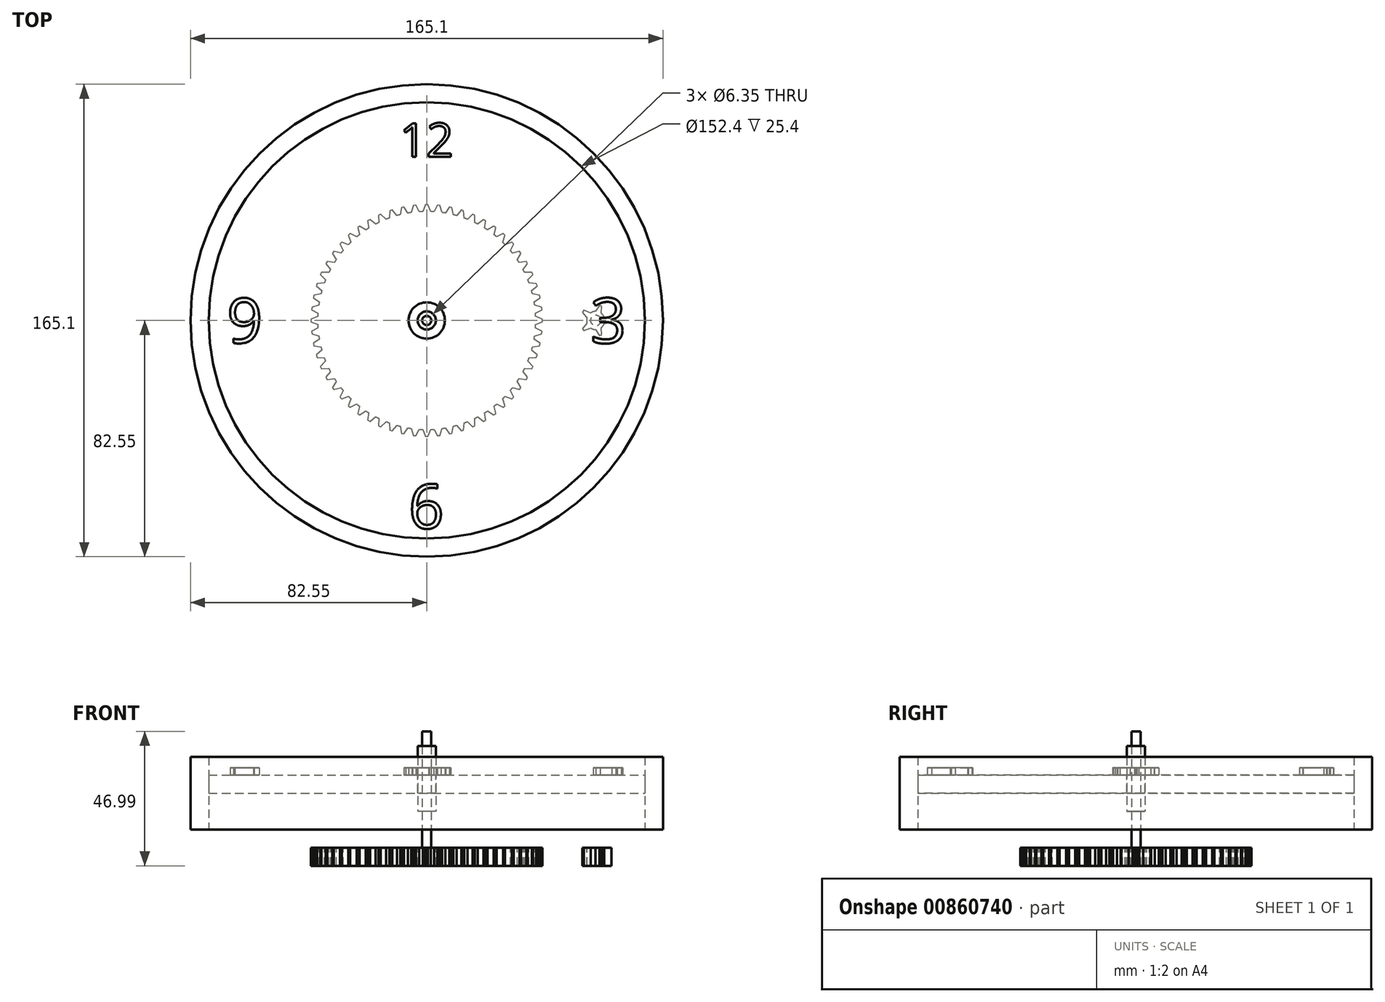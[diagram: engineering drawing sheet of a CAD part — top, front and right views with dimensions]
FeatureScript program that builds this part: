
annotation { "Feature Type Name" : "Feature", "Feature Type Description" : "" }
export const myFeature = defineFeature(function(context is Context, id is Id, definition is map)
    precondition{}
    {
        {
            var Q0;
            Q0=qCreatedBy(makeId("Front.planeOp"),FACE);
            var sketch = newSketch(context, id + "F0", { "sketchPlane" : qUnion([Q0])});
            skLineSegment(sketch, "E0.bottom", {"start": v(0, 0) * mm, "end": v(-76.2, 0) * mm});
            skLineSegment(sketch, "E0.top", {"start": v(0, 6.35) * mm, "end": v(-76.2, 6.35) * mm});
            skLineSegment(sketch, "E0.left", {"start": v(0, 0) * mm, "end": v(0, 6.35) * mm});
            skLineSegment(sketch, "E0.right", {"start": v(-76.2, 0) * mm, "end": v(-76.2, 6.35) * mm});
            skLineSegment(sketch, "E1.bottom", {"start": v(-82.55, 12.7) * mm, "end": v(-76.2, 12.7) * mm});
            skLineSegment(sketch, "E1.top", {"start": v(-82.55, -12.7) * mm, "end": v(-76.2, -12.7) * mm});
            skLineSegment(sketch, "E1.left", {"start": v(-82.55, 12.7) * mm, "end": v(-82.55, -12.7) * mm});
            skLineSegment(sketch, "E1.right", {"start": v(-76.2, 12.7) * mm, "end": v(-76.2, -12.7) * mm});
            skSolve(sketch);
        }
        {
            var Q0;
            {var subQ0=sQuery(id+"F0.wireOp",EDGE,"E0.bottom");Q0=makeQuery(id+"F0.imprint","IMPRINT",FACE,{"disambiguationData":[TD([[makeQuery(id+"F0.imprint","IMPRINT",EDGE,{"derivedFrom":subQ0}),-1.0]])]});}
            var Q1;
            Q1=sQuery(id+"F0.wireOp",EDGE,"E0.left");
            revolve(context, id + "F1", {"surfaceOperationType" : NewSurfaceOperationType.NEW, "entities" : qUnion([Q0]), "axis" : qUnion([Q1]), "revolveType" : RevolveType.FULL});
        }
        {
            var Q0;
            {var subQ2=sQuery(id+"F0.wireOp",EDGE,"E1.bottom");Q0=makeQuery(id+"F0.imprint","IMPRINT",FACE,{"disambiguationData":[TD([[makeQuery(id+"F0.imprint","IMPRINT",EDGE,{"derivedFrom":subQ2}),-1.0]])]});}
            var Q1;
            Q1=sQuery(id+"F0.wireOp",EDGE,"E0.left");
            revolve(context, id + "F2", {"surfaceOperationType" : NewSurfaceOperationType.NEW, "entities" : qUnion([Q0]), "axis" : qUnion([Q1]), "revolveType" : RevolveType.FULL});
        }
        {
            var Q0;
            Q0=makeQuery(id+"F1.opRevolve","SWEPT_FACE",FACE,{"disambiguationData":[OSD([sQuery(id+"F0.wireOp",EDGE,"E0.top")])]});
            var sketch = newSketch(context, id + "F3", { "sketchPlane" : qUnion([Q0])});
            skText(sketch, "E2", { "text": "12", "fontName": "OpenSans-Regular.ttf"});
            skText(sketch, "E3", { "text": "3", "fontName": "OpenSans-Regular.ttf"});
            skPoint(sketch, "E4", {"position": v(57.15, 0) * mm});
            skText(sketch, "E5", { "text": "6", "fontName": "OpenSans-Regular.ttf"});
            skText(sketch, "E6", { "text": "9", "fontName": "OpenSans-Regular.ttf"});
            skPoint(sketch, "E7", {"position": v(-57.15, 0) * mm});
            skCircle(sketch, "E8", {"center": v(0, 0) * mm, "radius": 6.35 * mm});
            skCircle(sketch, "E9", {"center": v(0, 0) * mm, "radius": 3.18 * mm});
            skCircle(sketch, "E10", {"center": v(0, 0) * mm, "radius": 1.59 * mm});
            const initialGuessF3  = {"E2": [-0.00953, 0.05715, 1, 0, 0.01188], "E3": [0.05715, -0.00791, 1, 0, 0.01582], "E5": [-0.00635, -0.0727, 1, 0, 0.01556], "E6": [-0.06985, -0.00784, 1, 0, 0.01569]};
            skSetInitialGuess(sketch, initialGuessF3);
            skSolve(sketch);
        }
        {
            var Q0;
            Q0 = qSketchRegion(id + "F3", true);
            extrude(context, id + "F4", {"entities" : qUnion([Q0]), "depth" : 2.54 * mm, "offsetDistance" : 25.4 * mm});
        }
        {
            var Q0;
            Q0=makeQuery(id+"F3.imprint","IMPRINT",FACE,{"disambiguationData":[TD([[makeQuery(id+"F3.imprint","IMPRINT",EDGE,{"derivedFrom":sQuery(id+"F3.wireOp",EDGE,"E9")}),1.0]])]});
            var Q1;
            Q1=makeQuery(id+"F3.imprint","IMPRINT",FACE,{"disambiguationData":[TD([[makeQuery(id+"F3.imprint","IMPRINT",EDGE,{"derivedFrom":sQuery(id+"F3.wireOp",EDGE,"E10")}),1.0]])]});
            extrude(context, id + "F5", {"entities" : qUnion([Q0, Q1]), "operationType" : NewBodyOperationType.REMOVE, "oppositeDirection" : true, "depth" : 6.35 * mm, "offsetDistance" : 25.4 * mm});
        }
        {
            var Q0;
            Q0=makeQuery(id+"F3.imprint","IMPRINT",FACE,{"disambiguationData":[TD([[makeQuery(id+"F3.imprint","IMPRINT",EDGE,{"derivedFrom":sQuery(id+"F3.wireOp",EDGE,"E9")}),1.0]])]});
            extrude(context, id + "F6", {"entities" : qUnion([Q0]), "depth" : 10.16 * mm, "offsetDistance" : 25.4 * mm, "hasSecondDirection" : true, "secondDirectionOppositeDirection" : true, "secondDirectionDepth" : 12.7 * mm});
        }
        {
            var Q0;
            Q0=makeQuery(id+"F3.imprint","IMPRINT",FACE,{"disambiguationData":[TD([[makeQuery(id+"F3.imprint","IMPRINT",EDGE,{"derivedFrom":sQuery(id+"F3.wireOp",EDGE,"E10")}),1.0]])]});
            extrude(context, id + "F7", {"entities" : qUnion([Q0]), "depth" : 15.24 * mm, "offsetDistance" : 25.4 * mm, "hasSecondDirection" : true, "secondDirectionOppositeDirection" : true, "secondDirectionDepth" : 25.4 * mm});
        }
        {
            var Q0;
            Q0=makeQuery(id+"F7.opExtrude","CAP_FACE",FACE,{"disambiguationData":[OSD([sQuery(id+"F3.wireOp",EDGE,"E10")])],"isStart":true});
            var sketch = newSketch(context, id + "F8", { "sketchPlane" : qUnion([Q0])});
            skCircle(sketch, "E11", {"center": v(0, 0) * mm, "radius": 38.1 * mm});
            skCircle(sketch, "E12", {"center": v(59.06, 0) * mm, "radius": 3.18 * mm});
            skLineSegment(sketch, "E13", {"start": v(-1.4, 38.07) * mm, "end": v(-0.44, 40.43) * mm});
            skLineSegment(sketch, "E14", {"start": v(-0.44, 40.43) * mm, "end": v(0.44, 40.43) * mm});
            skLineSegment(sketch, "E15", {"start": v(0.44, 40.43) * mm, "end": v(1.4, 38.07) * mm});
            skPoint(sketch, "E16", {"position": v(0, 40.43) * mm});
            skLineSegment(sketch, "E17.1.0", {"start": v(-5.37, 37.72) * mm, "end": v(-4.67, 40.16) * mm});
            skLineSegment(sketch, "E17.1.1", {"start": v(-4.67, 40.16) * mm, "end": v(-3.78, 40.25) * mm});
            skLineSegment(sketch, "E17.1.2", {"start": v(-3.78, 40.25) * mm, "end": v(-2.6, 38.01) * mm});
            skLineSegment(sketch, "E17.2.0", {"start": v(-9.28, 36.95) * mm, "end": v(-8.84, 39.45) * mm});
            skLineSegment(sketch, "E17.2.1", {"start": v(-8.84, 39.45) * mm, "end": v(-7.97, 39.64) * mm});
            skLineSegment(sketch, "E17.2.2", {"start": v(-7.97, 39.64) * mm, "end": v(-6.55, 37.53) * mm});
            skLineSegment(sketch, "E17.3.0", {"start": v(-13.1, 35.78) * mm, "end": v(-12.92, 38.31) * mm});
            skLineSegment(sketch, "E17.3.1", {"start": v(-12.92, 38.31) * mm, "end": v(-12.07, 38.59) * mm});
            skLineSegment(sketch, "E17.3.2", {"start": v(-12.07, 38.59) * mm, "end": v(-10.44, 36.64) * mm});
            skLineSegment(sketch, "E17.4.0", {"start": v(-16.76, 34.21) * mm, "end": v(-16.85, 36.75) * mm});
            skLineSegment(sketch, "E17.4.1", {"start": v(-16.85, 36.75) * mm, "end": v(-16.04, 37.11) * mm});
            skLineSegment(sketch, "E17.4.2", {"start": v(-16.04, 37.11) * mm, "end": v(-14.21, 35.35) * mm});
            skLineSegment(sketch, "E17.5.0", {"start": v(-20.25, 32.27) * mm, "end": v(-20.6, 34.8) * mm});
            skLineSegment(sketch, "E17.5.1", {"start": v(-20.6, 34.8) * mm, "end": v(-19.83, 35.23) * mm});
            skLineSegment(sketch, "E17.5.2", {"start": v(-19.83, 35.23) * mm, "end": v(-17.83, 33.67) * mm});
            skLineSegment(sketch, "E17.6.0", {"start": v(-23.5, 29.98) * mm, "end": v(-24.12, 32.45) * mm});
            skLineSegment(sketch, "E17.6.1", {"start": v(-24.12, 32.45) * mm, "end": v(-23.4, 32.97) * mm});
            skLineSegment(sketch, "E17.6.2", {"start": v(-23.4, 32.97) * mm, "end": v(-21.25, 31.62) * mm});
            skLineSegment(sketch, "E17.7.0", {"start": v(-26.51, 27.36) * mm, "end": v(-27.38, 29.75) * mm});
            skLineSegment(sketch, "E17.7.1", {"start": v(-27.38, 29.75) * mm, "end": v(-26.72, 30.34) * mm});
            skLineSegment(sketch, "E17.7.2", {"start": v(-26.72, 30.34) * mm, "end": v(-24.44, 29.23) * mm});
            skLineSegment(sketch, "E17.8.0", {"start": v(-29.23, 24.44) * mm, "end": v(-30.34, 26.72) * mm});
            skLineSegment(sketch, "E17.8.1", {"start": v(-30.34, 26.72) * mm, "end": v(-29.75, 27.38) * mm});
            skLineSegment(sketch, "E17.8.2", {"start": v(-29.75, 27.38) * mm, "end": v(-27.36, 26.51) * mm});
            skLineSegment(sketch, "E17.9.0", {"start": v(-31.62, 21.25) * mm, "end": v(-32.97, 23.4) * mm});
            skLineSegment(sketch, "E17.9.1", {"start": v(-32.97, 23.4) * mm, "end": v(-32.45, 24.12) * mm});
            skLineSegment(sketch, "E17.9.2", {"start": v(-32.45, 24.12) * mm, "end": v(-29.98, 23.5) * mm});
            skLineSegment(sketch, "E17.10.0", {"start": v(-33.67, 17.83) * mm, "end": v(-35.23, 19.83) * mm});
            skLineSegment(sketch, "E17.10.1", {"start": v(-35.23, 19.83) * mm, "end": v(-34.8, 20.6) * mm});
            skLineSegment(sketch, "E17.10.2", {"start": v(-34.8, 20.6) * mm, "end": v(-32.27, 20.25) * mm});
            skLineSegment(sketch, "E17.11.0", {"start": v(-35.35, 14.21) * mm, "end": v(-37.11, 16.04) * mm});
            skLineSegment(sketch, "E17.11.1", {"start": v(-37.11, 16.04) * mm, "end": v(-36.75, 16.85) * mm});
            skLineSegment(sketch, "E17.11.2", {"start": v(-36.75, 16.85) * mm, "end": v(-34.21, 16.76) * mm});
            skLineSegment(sketch, "E17.12.0", {"start": v(-36.64, 10.44) * mm, "end": v(-38.59, 12.07) * mm});
            skLineSegment(sketch, "E17.12.1", {"start": v(-38.59, 12.07) * mm, "end": v(-38.31, 12.92) * mm});
            skLineSegment(sketch, "E17.12.2", {"start": v(-38.31, 12.92) * mm, "end": v(-35.78, 13.1) * mm});
            skLineSegment(sketch, "E17.13.0", {"start": v(-37.53, 6.55) * mm, "end": v(-39.64, 7.97) * mm});
            skLineSegment(sketch, "E17.13.1", {"start": v(-39.64, 7.97) * mm, "end": v(-39.45, 8.84) * mm});
            skLineSegment(sketch, "E17.13.2", {"start": v(-39.45, 8.84) * mm, "end": v(-36.95, 9.28) * mm});
            skLineSegment(sketch, "E17.14.0", {"start": v(-38.01, 2.6) * mm, "end": v(-40.25, 3.78) * mm});
            skLineSegment(sketch, "E17.14.1", {"start": v(-40.25, 3.78) * mm, "end": v(-40.16, 4.67) * mm});
            skLineSegment(sketch, "E17.14.2", {"start": v(-40.16, 4.67) * mm, "end": v(-37.72, 5.37) * mm});
            skLineSegment(sketch, "E17.15.0", {"start": v(-38.07, -1.4) * mm, "end": v(-40.43, -0.44) * mm});
            skLineSegment(sketch, "E17.15.1", {"start": v(-40.43, -0.44) * mm, "end": v(-40.43, 0.44) * mm});
            skLineSegment(sketch, "E17.15.2", {"start": v(-40.43, 0.44) * mm, "end": v(-38.07, 1.4) * mm});
            skLineSegment(sketch, "E17.16.0", {"start": v(-37.72, -5.37) * mm, "end": v(-40.16, -4.67) * mm});
            skLineSegment(sketch, "E17.16.1", {"start": v(-40.16, -4.67) * mm, "end": v(-40.25, -3.78) * mm});
            skLineSegment(sketch, "E17.16.2", {"start": v(-40.25, -3.78) * mm, "end": v(-38.01, -2.6) * mm});
            skLineSegment(sketch, "E17.17.0", {"start": v(-36.95, -9.28) * mm, "end": v(-39.45, -8.84) * mm});
            skLineSegment(sketch, "E17.17.1", {"start": v(-39.45, -8.84) * mm, "end": v(-39.64, -7.97) * mm});
            skLineSegment(sketch, "E17.17.2", {"start": v(-39.64, -7.97) * mm, "end": v(-37.53, -6.55) * mm});
            skLineSegment(sketch, "E17.18.0", {"start": v(-35.78, -13.1) * mm, "end": v(-38.31, -12.92) * mm});
            skLineSegment(sketch, "E17.18.1", {"start": v(-38.31, -12.92) * mm, "end": v(-38.59, -12.07) * mm});
            skLineSegment(sketch, "E17.18.2", {"start": v(-38.59, -12.07) * mm, "end": v(-36.64, -10.44) * mm});
            skLineSegment(sketch, "E17.19.0", {"start": v(-34.21, -16.76) * mm, "end": v(-36.75, -16.85) * mm});
            skLineSegment(sketch, "E17.19.1", {"start": v(-36.75, -16.85) * mm, "end": v(-37.11, -16.04) * mm});
            skLineSegment(sketch, "E17.19.2", {"start": v(-37.11, -16.04) * mm, "end": v(-35.35, -14.21) * mm});
            skLineSegment(sketch, "E17.20.0", {"start": v(-32.27, -20.25) * mm, "end": v(-34.8, -20.6) * mm});
            skLineSegment(sketch, "E17.20.1", {"start": v(-34.8, -20.6) * mm, "end": v(-35.23, -19.83) * mm});
            skLineSegment(sketch, "E17.20.2", {"start": v(-35.23, -19.83) * mm, "end": v(-33.67, -17.83) * mm});
            skLineSegment(sketch, "E17.21.0", {"start": v(-29.98, -23.5) * mm, "end": v(-32.45, -24.12) * mm});
            skLineSegment(sketch, "E17.21.1", {"start": v(-32.45, -24.12) * mm, "end": v(-32.97, -23.4) * mm});
            skLineSegment(sketch, "E17.21.2", {"start": v(-32.97, -23.4) * mm, "end": v(-31.62, -21.25) * mm});
            skLineSegment(sketch, "E17.22.0", {"start": v(-27.36, -26.51) * mm, "end": v(-29.75, -27.38) * mm});
            skLineSegment(sketch, "E17.22.1", {"start": v(-29.75, -27.38) * mm, "end": v(-30.34, -26.72) * mm});
            skLineSegment(sketch, "E17.22.2", {"start": v(-30.34, -26.72) * mm, "end": v(-29.23, -24.44) * mm});
            skLineSegment(sketch, "E17.23.0", {"start": v(-24.44, -29.23) * mm, "end": v(-26.72, -30.34) * mm});
            skLineSegment(sketch, "E17.23.1", {"start": v(-26.72, -30.34) * mm, "end": v(-27.38, -29.75) * mm});
            skLineSegment(sketch, "E17.23.2", {"start": v(-27.38, -29.75) * mm, "end": v(-26.51, -27.36) * mm});
            skLineSegment(sketch, "E17.24.0", {"start": v(-21.25, -31.62) * mm, "end": v(-23.4, -32.97) * mm});
            skLineSegment(sketch, "E17.24.1", {"start": v(-23.4, -32.97) * mm, "end": v(-24.12, -32.45) * mm});
            skLineSegment(sketch, "E17.24.2", {"start": v(-24.12, -32.45) * mm, "end": v(-23.5, -29.98) * mm});
            skLineSegment(sketch, "E17.25.0", {"start": v(-17.83, -33.67) * mm, "end": v(-19.83, -35.23) * mm});
            skLineSegment(sketch, "E17.25.1", {"start": v(-19.83, -35.23) * mm, "end": v(-20.6, -34.8) * mm});
            skLineSegment(sketch, "E17.25.2", {"start": v(-20.6, -34.8) * mm, "end": v(-20.25, -32.27) * mm});
            skLineSegment(sketch, "E17.26.0", {"start": v(-14.21, -35.35) * mm, "end": v(-16.04, -37.11) * mm});
            skLineSegment(sketch, "E17.26.1", {"start": v(-16.04, -37.11) * mm, "end": v(-16.85, -36.75) * mm});
            skLineSegment(sketch, "E17.26.2", {"start": v(-16.85, -36.75) * mm, "end": v(-16.76, -34.21) * mm});
            skLineSegment(sketch, "E17.27.0", {"start": v(-10.44, -36.64) * mm, "end": v(-12.07, -38.59) * mm});
            skLineSegment(sketch, "E17.27.1", {"start": v(-12.07, -38.59) * mm, "end": v(-12.92, -38.31) * mm});
            skLineSegment(sketch, "E17.27.2", {"start": v(-12.92, -38.31) * mm, "end": v(-13.1, -35.78) * mm});
            skLineSegment(sketch, "E17.28.0", {"start": v(-6.55, -37.53) * mm, "end": v(-7.97, -39.64) * mm});
            skLineSegment(sketch, "E17.28.1", {"start": v(-7.97, -39.64) * mm, "end": v(-8.84, -39.45) * mm});
            skLineSegment(sketch, "E17.28.2", {"start": v(-8.84, -39.45) * mm, "end": v(-9.28, -36.95) * mm});
            skLineSegment(sketch, "E17.29.0", {"start": v(-2.6, -38.01) * mm, "end": v(-3.78, -40.25) * mm});
            skLineSegment(sketch, "E17.29.1", {"start": v(-3.78, -40.25) * mm, "end": v(-4.67, -40.16) * mm});
            skLineSegment(sketch, "E17.29.2", {"start": v(-4.67, -40.16) * mm, "end": v(-5.37, -37.72) * mm});
            skLineSegment(sketch, "E17.30.0", {"start": v(1.4, -38.07) * mm, "end": v(0.44, -40.43) * mm});
            skLineSegment(sketch, "E17.30.1", {"start": v(0.44, -40.43) * mm, "end": v(-0.44, -40.43) * mm});
            skLineSegment(sketch, "E17.30.2", {"start": v(-0.44, -40.43) * mm, "end": v(-1.4, -38.07) * mm});
            skLineSegment(sketch, "E17.31.0", {"start": v(5.37, -37.72) * mm, "end": v(4.67, -40.16) * mm});
            skLineSegment(sketch, "E17.31.1", {"start": v(4.67, -40.16) * mm, "end": v(3.78, -40.25) * mm});
            skLineSegment(sketch, "E17.31.2", {"start": v(3.78, -40.25) * mm, "end": v(2.6, -38.01) * mm});
            skLineSegment(sketch, "E17.32.0", {"start": v(9.28, -36.95) * mm, "end": v(8.84, -39.45) * mm});
            skLineSegment(sketch, "E17.32.1", {"start": v(8.84, -39.45) * mm, "end": v(7.97, -39.64) * mm});
            skLineSegment(sketch, "E17.32.2", {"start": v(7.97, -39.64) * mm, "end": v(6.55, -37.53) * mm});
            skLineSegment(sketch, "E17.33.0", {"start": v(13.1, -35.78) * mm, "end": v(12.92, -38.31) * mm});
            skLineSegment(sketch, "E17.33.1", {"start": v(12.92, -38.31) * mm, "end": v(12.07, -38.59) * mm});
            skLineSegment(sketch, "E17.33.2", {"start": v(12.07, -38.59) * mm, "end": v(10.44, -36.64) * mm});
            skLineSegment(sketch, "E17.34.0", {"start": v(16.76, -34.21) * mm, "end": v(16.85, -36.75) * mm});
            skLineSegment(sketch, "E17.34.1", {"start": v(16.85, -36.75) * mm, "end": v(16.04, -37.11) * mm});
            skLineSegment(sketch, "E17.34.2", {"start": v(16.04, -37.11) * mm, "end": v(14.21, -35.35) * mm});
            skLineSegment(sketch, "E17.35.0", {"start": v(20.25, -32.27) * mm, "end": v(20.6, -34.8) * mm});
            skLineSegment(sketch, "E17.35.1", {"start": v(20.6, -34.8) * mm, "end": v(19.83, -35.23) * mm});
            skLineSegment(sketch, "E17.35.2", {"start": v(19.83, -35.23) * mm, "end": v(17.83, -33.67) * mm});
            skLineSegment(sketch, "E17.36.0", {"start": v(23.5, -29.98) * mm, "end": v(24.12, -32.45) * mm});
            skLineSegment(sketch, "E17.36.1", {"start": v(24.12, -32.45) * mm, "end": v(23.4, -32.97) * mm});
            skLineSegment(sketch, "E17.36.2", {"start": v(23.4, -32.97) * mm, "end": v(21.25, -31.62) * mm});
            skLineSegment(sketch, "E17.37.0", {"start": v(26.51, -27.36) * mm, "end": v(27.38, -29.75) * mm});
            skLineSegment(sketch, "E17.37.1", {"start": v(27.38, -29.75) * mm, "end": v(26.72, -30.34) * mm});
            skLineSegment(sketch, "E17.37.2", {"start": v(26.72, -30.34) * mm, "end": v(24.44, -29.23) * mm});
            skLineSegment(sketch, "E17.38.0", {"start": v(29.23, -24.44) * mm, "end": v(30.34, -26.72) * mm});
            skLineSegment(sketch, "E17.38.1", {"start": v(30.34, -26.72) * mm, "end": v(29.75, -27.38) * mm});
            skLineSegment(sketch, "E17.38.2", {"start": v(29.75, -27.38) * mm, "end": v(27.36, -26.51) * mm});
            skLineSegment(sketch, "E17.39.0", {"start": v(31.62, -21.25) * mm, "end": v(32.97, -23.4) * mm});
            skLineSegment(sketch, "E17.39.1", {"start": v(32.97, -23.4) * mm, "end": v(32.45, -24.12) * mm});
            skLineSegment(sketch, "E17.39.2", {"start": v(32.45, -24.12) * mm, "end": v(29.98, -23.5) * mm});
            skLineSegment(sketch, "E17.40.0", {"start": v(33.67, -17.83) * mm, "end": v(35.23, -19.83) * mm});
            skLineSegment(sketch, "E17.40.1", {"start": v(35.23, -19.83) * mm, "end": v(34.8, -20.6) * mm});
            skLineSegment(sketch, "E17.40.2", {"start": v(34.8, -20.6) * mm, "end": v(32.27, -20.25) * mm});
            skLineSegment(sketch, "E17.41.0", {"start": v(35.35, -14.21) * mm, "end": v(37.11, -16.04) * mm});
            skLineSegment(sketch, "E17.41.1", {"start": v(37.11, -16.04) * mm, "end": v(36.75, -16.85) * mm});
            skLineSegment(sketch, "E17.41.2", {"start": v(36.75, -16.85) * mm, "end": v(34.21, -16.76) * mm});
            skLineSegment(sketch, "E17.42.0", {"start": v(36.64, -10.44) * mm, "end": v(38.59, -12.07) * mm});
            skLineSegment(sketch, "E17.42.1", {"start": v(38.59, -12.07) * mm, "end": v(38.31, -12.92) * mm});
            skLineSegment(sketch, "E17.42.2", {"start": v(38.31, -12.92) * mm, "end": v(35.78, -13.1) * mm});
            skLineSegment(sketch, "E17.43.0", {"start": v(37.53, -6.55) * mm, "end": v(39.64, -7.97) * mm});
            skLineSegment(sketch, "E17.43.1", {"start": v(39.64, -7.97) * mm, "end": v(39.45, -8.84) * mm});
            skLineSegment(sketch, "E17.43.2", {"start": v(39.45, -8.84) * mm, "end": v(36.95, -9.28) * mm});
            skLineSegment(sketch, "E17.44.0", {"start": v(38.01, -2.6) * mm, "end": v(40.25, -3.78) * mm});
            skLineSegment(sketch, "E17.44.1", {"start": v(40.25, -3.78) * mm, "end": v(40.16, -4.67) * mm});
            skLineSegment(sketch, "E17.44.2", {"start": v(40.16, -4.67) * mm, "end": v(37.72, -5.37) * mm});
            skLineSegment(sketch, "E17.45.0", {"start": v(38.07, 1.4) * mm, "end": v(40.43, 0.44) * mm});
            skLineSegment(sketch, "E17.45.1", {"start": v(40.43, 0.44) * mm, "end": v(40.43, -0.44) * mm});
            skLineSegment(sketch, "E17.45.2", {"start": v(40.43, -0.44) * mm, "end": v(38.07, -1.4) * mm});
            skLineSegment(sketch, "E17.46.0", {"start": v(37.72, 5.37) * mm, "end": v(40.16, 4.67) * mm});
            skLineSegment(sketch, "E17.46.1", {"start": v(40.16, 4.67) * mm, "end": v(40.25, 3.78) * mm});
            skLineSegment(sketch, "E17.46.2", {"start": v(40.25, 3.78) * mm, "end": v(38.01, 2.6) * mm});
            skLineSegment(sketch, "E17.47.0", {"start": v(36.95, 9.28) * mm, "end": v(39.45, 8.84) * mm});
            skLineSegment(sketch, "E17.47.1", {"start": v(39.45, 8.84) * mm, "end": v(39.64, 7.97) * mm});
            skLineSegment(sketch, "E17.47.2", {"start": v(39.64, 7.97) * mm, "end": v(37.53, 6.55) * mm});
            skLineSegment(sketch, "E17.48.0", {"start": v(35.78, 13.1) * mm, "end": v(38.31, 12.92) * mm});
            skLineSegment(sketch, "E17.48.1", {"start": v(38.31, 12.92) * mm, "end": v(38.59, 12.07) * mm});
            skLineSegment(sketch, "E17.48.2", {"start": v(38.59, 12.07) * mm, "end": v(36.64, 10.44) * mm});
            skLineSegment(sketch, "E17.49.0", {"start": v(34.21, 16.76) * mm, "end": v(36.75, 16.85) * mm});
            skLineSegment(sketch, "E17.49.1", {"start": v(36.75, 16.85) * mm, "end": v(37.11, 16.04) * mm});
            skLineSegment(sketch, "E17.49.2", {"start": v(37.11, 16.04) * mm, "end": v(35.35, 14.21) * mm});
            skLineSegment(sketch, "E17.50.0", {"start": v(32.27, 20.25) * mm, "end": v(34.8, 20.6) * mm});
            skLineSegment(sketch, "E17.50.1", {"start": v(34.8, 20.6) * mm, "end": v(35.23, 19.83) * mm});
            skLineSegment(sketch, "E17.50.2", {"start": v(35.23, 19.83) * mm, "end": v(33.67, 17.83) * mm});
            skLineSegment(sketch, "E17.51.0", {"start": v(29.98, 23.5) * mm, "end": v(32.45, 24.12) * mm});
            skLineSegment(sketch, "E17.51.1", {"start": v(32.45, 24.12) * mm, "end": v(32.97, 23.4) * mm});
            skLineSegment(sketch, "E17.51.2", {"start": v(32.97, 23.4) * mm, "end": v(31.62, 21.25) * mm});
            skLineSegment(sketch, "E17.52.0", {"start": v(27.36, 26.51) * mm, "end": v(29.75, 27.38) * mm});
            skLineSegment(sketch, "E17.52.1", {"start": v(29.75, 27.38) * mm, "end": v(30.34, 26.72) * mm});
            skLineSegment(sketch, "E17.52.2", {"start": v(30.34, 26.72) * mm, "end": v(29.23, 24.44) * mm});
            skLineSegment(sketch, "E17.53.0", {"start": v(24.44, 29.23) * mm, "end": v(26.72, 30.34) * mm});
            skLineSegment(sketch, "E17.53.1", {"start": v(26.72, 30.34) * mm, "end": v(27.38, 29.75) * mm});
            skLineSegment(sketch, "E17.53.2", {"start": v(27.38, 29.75) * mm, "end": v(26.51, 27.36) * mm});
            skLineSegment(sketch, "E17.54.0", {"start": v(21.25, 31.62) * mm, "end": v(23.4, 32.97) * mm});
            skLineSegment(sketch, "E17.54.1", {"start": v(23.4, 32.97) * mm, "end": v(24.12, 32.45) * mm});
            skLineSegment(sketch, "E17.54.2", {"start": v(24.12, 32.45) * mm, "end": v(23.5, 29.98) * mm});
            skLineSegment(sketch, "E17.55.0", {"start": v(17.83, 33.67) * mm, "end": v(19.83, 35.23) * mm});
            skLineSegment(sketch, "E17.55.1", {"start": v(19.83, 35.23) * mm, "end": v(20.6, 34.8) * mm});
            skLineSegment(sketch, "E17.55.2", {"start": v(20.6, 34.8) * mm, "end": v(20.25, 32.27) * mm});
            skLineSegment(sketch, "E17.56.0", {"start": v(14.21, 35.35) * mm, "end": v(16.04, 37.11) * mm});
            skLineSegment(sketch, "E17.56.1", {"start": v(16.04, 37.11) * mm, "end": v(16.85, 36.75) * mm});
            skLineSegment(sketch, "E17.56.2", {"start": v(16.85, 36.75) * mm, "end": v(16.76, 34.21) * mm});
            skLineSegment(sketch, "E17.57.0", {"start": v(10.44, 36.64) * mm, "end": v(12.07, 38.59) * mm});
            skLineSegment(sketch, "E17.57.1", {"start": v(12.07, 38.59) * mm, "end": v(12.92, 38.31) * mm});
            skLineSegment(sketch, "E17.57.2", {"start": v(12.92, 38.31) * mm, "end": v(13.1, 35.78) * mm});
            skLineSegment(sketch, "E17.58.0", {"start": v(6.55, 37.53) * mm, "end": v(7.97, 39.64) * mm});
            skLineSegment(sketch, "E17.58.1", {"start": v(7.97, 39.64) * mm, "end": v(8.84, 39.45) * mm});
            skLineSegment(sketch, "E17.58.2", {"start": v(8.84, 39.45) * mm, "end": v(9.28, 36.95) * mm});
            skLineSegment(sketch, "E17.59.0", {"start": v(2.6, 38.01) * mm, "end": v(3.78, 40.25) * mm});
            skLineSegment(sketch, "E17.59.1", {"start": v(3.78, 40.25) * mm, "end": v(4.67, 40.16) * mm});
            skLineSegment(sketch, "E17.59.2", {"start": v(4.67, 40.16) * mm, "end": v(5.37, 37.72) * mm});
            skCircle(sketch, "E18.0", {"center": v(0, 0) * mm, "radius": 3.18 * mm});
            skCircle(sketch, "E19", {"center": v(59.06, 0) * mm, "radius": 1.83 * mm});
            skLineSegment(sketch, "E20", {"start": v(62.04, 1.1) * mm, "end": v(64.5, 0.44) * mm});
            skLineSegment(sketch, "E21", {"start": v(64.5, 0.44) * mm, "end": v(64.5, -0.44) * mm});
            skLineSegment(sketch, "E22", {"start": v(64.5, -0.44) * mm, "end": v(62.04, -1.1) * mm});
            skPoint(sketch, "E23", {"position": v(64.5, 0) * mm});
            skLineSegment(sketch, "E24.1.0", {"start": v(58.94, 3.17) * mm, "end": v(60.32, 5.3) * mm});
            skLineSegment(sketch, "E24.1.1", {"start": v(60.32, 5.3) * mm, "end": v(61.16, 5.03) * mm});
            skLineSegment(sketch, "E24.1.2", {"start": v(61.16, 5.03) * mm, "end": v(61.03, 2.5) * mm});
            skLineSegment(sketch, "E24.2.0", {"start": v(56, 0.86) * mm, "end": v(54.4, 2.83) * mm});
            skLineSegment(sketch, "E24.2.1", {"start": v(54.4, 2.83) * mm, "end": v(54.93, 3.55) * mm});
            skLineSegment(sketch, "E24.2.2", {"start": v(54.93, 3.55) * mm, "end": v(57.3, 2.64) * mm});
            skLineSegment(sketch, "E24.3.0", {"start": v(57.3, -2.64) * mm, "end": v(54.93, -3.55) * mm});
            skLineSegment(sketch, "E24.3.1", {"start": v(54.93, -3.55) * mm, "end": v(54.4, -2.83) * mm});
            skLineSegment(sketch, "E24.3.2", {"start": v(54.4, -2.83) * mm, "end": v(56, -0.86) * mm});
            skLineSegment(sketch, "E24.4.0", {"start": v(61.03, -2.5) * mm, "end": v(61.16, -5.03) * mm});
            skLineSegment(sketch, "E24.4.1", {"start": v(61.16, -5.03) * mm, "end": v(60.32, -5.3) * mm});
            skLineSegment(sketch, "E24.4.2", {"start": v(60.32, -5.3) * mm, "end": v(58.94, -3.17) * mm});
            skSolve(sketch);
        }
        {
            var Q0;
            Q0 = qSketchRegion(id + "F8", true);
            extrude(context, id + "F9", {"entities" : qUnion([Q0]), "depth" : 6.35 * mm, "offsetDistance" : 25.4 * mm});
        }
    });
